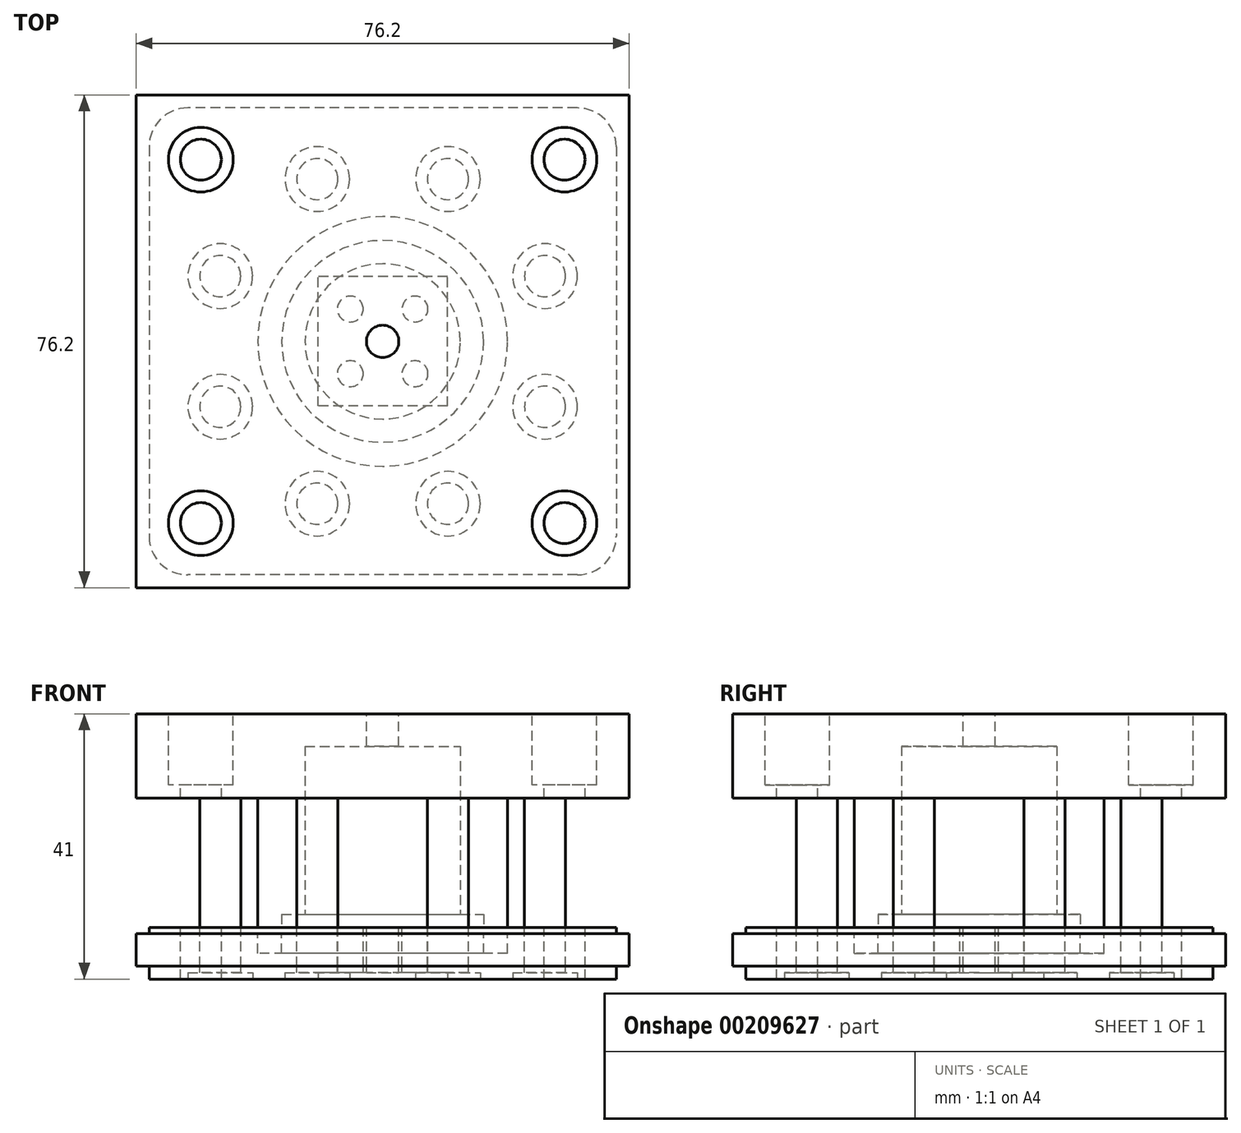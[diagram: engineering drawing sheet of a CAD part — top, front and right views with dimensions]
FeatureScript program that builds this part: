
annotation { "Feature Type Name" : "Feature", "Feature Type Description" : "" }
export const myFeature = defineFeature(function(context is Context, id is Id, definition is map)
    precondition{}
    {
        {
            var Q0;
            Q0=qCreatedBy(makeId("Top.planeOp"),FACE);
            var sketch = newSketch(context, id + "F0", { "sketchPlane" : qUnion([Q0])});
            skLineSegment(sketch, "E0.bottom", {"start": v(36.1, 36.1) * mm, "end": v(-36.1, 36.1) * mm});
            skLineSegment(sketch, "E0.top", {"start": v(36.1, -36.1) * mm, "end": v(-36.1, -36.1) * mm});
            skLineSegment(sketch, "E0.left", {"start": v(36.1, 36.1) * mm, "end": v(36.1, -36.1) * mm});
            skLineSegment(sketch, "E0.right", {"start": v(-36.1, 36.1) * mm, "end": v(-36.1, -36.1) * mm});
            skPoint(sketch, "E0.middle", {"position": v(0, 0) * mm});
            skSolve(sketch);
        }
        {
            var Q0;
            Q0=makeQuery(id+"F0.imprint","IMPRINT",FACE,{"disambiguationData":[TD([[makeQuery(id+"F0.imprint","IMPRINT",EDGE,{"derivedFrom":sQuery(id+"F0.wireOp",EDGE,"E0.bottom")}),1.0]])]});
            extrude(context, id + "F1", {"entities" : qUnion([Q0]), "depth" : 2 * mm});
        }
        {
            var Q0;
            Q0=makeQuery(id+"F1.opExtrude","SWEPT_EDGE",EDGE,{"disambiguationData":[OSD([sQuery(id+"F0.wireOp",EDGE,"E0.top"),sQuery(id+"F0.wireOp",EDGE,"E0.right")])]});
            var Q1;
            Q1=makeQuery(id+"F1.opExtrude","SWEPT_EDGE",EDGE,{"disambiguationData":[OSD([sQuery(id+"F0.wireOp",EDGE,"E0.top"),sQuery(id+"F0.wireOp",EDGE,"E0.left")])]});
            var Q2;
            Q2=makeQuery(id+"F1.opExtrude","SWEPT_EDGE",EDGE,{"disambiguationData":[OSD([sQuery(id+"F0.wireOp",EDGE,"E0.bottom"),sQuery(id+"F0.wireOp",EDGE,"E0.right")])]});
            var Q3;
            Q3=makeQuery(id+"F1.opExtrude","SWEPT_EDGE",EDGE,{"disambiguationData":[OSD([sQuery(id+"F0.wireOp",EDGE,"E0.bottom"),sQuery(id+"F0.wireOp",EDGE,"E0.left")])]});
            fillet(context, id + "F2", {"entities" : qUnion([Q0, Q1, Q2, Q3]), "radius" : 6 * mm, "tangentPropagation" : true, "allowEdgeOverflow" : false});
        }
        {
            var Q0;
            Q0=makeQuery(id+"F1.opExtrude","CAP_FACE",FACE,{"disambiguationData":[OSD([sQuery(id+"F0.wireOp",EDGE,"E0.bottom"),sQuery(id+"F0.wireOp",EDGE,"E0.top"),sQuery(id+"F0.wireOp",EDGE,"E0.left"),sQuery(id+"F0.wireOp",EDGE,"E0.right")])],"isStart":false});
            var sketch = newSketch(context, id + "F3", { "sketchPlane" : qUnion([Q0])});
            skLineSegment(sketch, "E1.bottom", {"start": v(10.1, 25.1) * mm, "end": v(-10.1, 25.1) * mm, "construction": true});
            skLineSegment(sketch, "E1.top", {"start": v(10.1, -25.1) * mm, "end": v(-10.1, -25.1) * mm});
            skLineSegment(sketch, "E1.left", {"start": v(10.1, 25.1) * mm, "end": v(10.1, -25.1) * mm, "construction": true});
            skLineSegment(sketch, "E1.right", {"start": v(-10.1, 25.1) * mm, "end": v(-10.1, -25.1) * mm, "construction": true});
            skPoint(sketch, "E1.middle", {"position": v(0, 0) * mm});
            skLineSegment(sketch, "E2.bottom", {"start": v(25.1, 10.1) * mm, "end": v(-25.1, 10.1) * mm, "construction": true});
            skLineSegment(sketch, "E2.top", {"start": v(25.1, -10.1) * mm, "end": v(-25.1, -10.1) * mm, "construction": true});
            skLineSegment(sketch, "E2.left", {"start": v(25.1, 10.1) * mm, "end": v(25.1, -10.1) * mm, "construction": true});
            skLineSegment(sketch, "E2.right", {"start": v(-25.1, 10.1) * mm, "end": v(-25.1, -10.1) * mm, "construction": true});
            skLineSegment(sketch, "E3.bottom", {"start": v(28.1, 28.1) * mm, "end": v(-28.1, 28.1) * mm, "construction": true});
            skLineSegment(sketch, "E3.top", {"start": v(28.1, -28.1) * mm, "end": v(-28.1, -28.1) * mm, "construction": true});
            skLineSegment(sketch, "E3.left", {"start": v(28.1, 28.1) * mm, "end": v(28.1, -28.1) * mm, "construction": true});
            skLineSegment(sketch, "E3.right", {"start": v(-28.1, 28.1) * mm, "end": v(-28.1, -28.1) * mm, "construction": true});
            skLineSegment(sketch, "E4.bottom", {"start": v(5, 5) * mm, "end": v(-5, 5) * mm, "construction": true});
            skLineSegment(sketch, "E4.top", {"start": v(5, -5) * mm, "end": v(-5, -5) * mm, "construction": true});
            skLineSegment(sketch, "E4.left", {"start": v(5, 5) * mm, "end": v(5, -5) * mm, "construction": true});
            skLineSegment(sketch, "E4.right", {"start": v(-5, 5) * mm, "end": v(-5, -5) * mm, "construction": true});
            skCircle(sketch, "E5", {"center": v(-28.1, 28.1) * mm, "radius": 3.18 * mm});
            skCircle(sketch, "E6", {"center": v(28.1, 28.1) * mm, "radius": 3.18 * mm});
            skCircle(sketch, "E7", {"center": v(28.1, -28.1) * mm, "radius": 3.18 * mm});
            skCircle(sketch, "E8", {"center": v(25.1, 10.1) * mm, "radius": 3.18 * mm});
            skCircle(sketch, "E9", {"center": v(25.1, -10.1) * mm, "radius": 3.18 * mm});
            skCircle(sketch, "E10", {"center": v(-25.1, -10.1) * mm, "radius": 3.18 * mm});
            skCircle(sketch, "E11", {"center": v(-25.1, 10.1) * mm, "radius": 3.18 * mm});
            skCircle(sketch, "E12", {"center": v(-28.1, -28.1) * mm, "radius": 3.18 * mm});
            skCircle(sketch, "E13", {"center": v(-10.1, 25.1) * mm, "radius": 3.18 * mm});
            skCircle(sketch, "E14", {"center": v(10.1, 25.1) * mm, "radius": 3.18 * mm});
            skCircle(sketch, "E15", {"center": v(10.1, -25.1) * mm, "radius": 3.18 * mm});
            skCircle(sketch, "E16", {"center": v(-10.1, -25.1) * mm, "radius": 3.18 * mm});
            skCircle(sketch, "E17", {"center": v(5, 5) * mm, "radius": 2 * mm});
            skCircle(sketch, "E18", {"center": v(-5, 5) * mm, "radius": 2 * mm});
            skCircle(sketch, "E19", {"center": v(-5, -5) * mm, "radius": 2 * mm});
            skCircle(sketch, "E20", {"center": v(5, -5) * mm, "radius": 2 * mm});
            skSolve(sketch);
        }
        {
            var Q0;
            Q0=makeQuery(id+"F3.imprint","IMPRINT",FACE,{"disambiguationData":[TD([[makeQuery(id+"F3.imprint","IMPRINT",EDGE,{"derivedFrom":sQuery(id+"F3.wireOp",EDGE,"E5")}),1.0]])]});
            var Q1;
            Q1=makeQuery(id+"F3.imprint","IMPRINT",FACE,{"disambiguationData":[TD([[makeQuery(id+"F3.imprint","IMPRINT",EDGE,{"derivedFrom":sQuery(id+"F3.wireOp",EDGE,"E13")}),1.0]])]});
            var Q2;
            Q2=makeQuery(id+"F3.imprint","IMPRINT",FACE,{"disambiguationData":[TD([[makeQuery(id+"F3.imprint","IMPRINT",EDGE,{"derivedFrom":sQuery(id+"F3.wireOp",EDGE,"E14")}),1.0]])]});
            var Q3;
            Q3=makeQuery(id+"F3.imprint","IMPRINT",FACE,{"disambiguationData":[TD([[makeQuery(id+"F3.imprint","IMPRINT",EDGE,{"derivedFrom":sQuery(id+"F3.wireOp",EDGE,"E6")}),1.0]])]});
            var Q4;
            Q4=makeQuery(id+"F3.imprint","IMPRINT",FACE,{"disambiguationData":[TD([[makeQuery(id+"F3.imprint","IMPRINT",EDGE,{"derivedFrom":sQuery(id+"F3.wireOp",EDGE,"E11")}),1.0]])]});
            var Q5;
            Q5=makeQuery(id+"F3.imprint","IMPRINT",FACE,{"disambiguationData":[TD([[makeQuery(id+"F3.imprint","IMPRINT",EDGE,{"derivedFrom":sQuery(id+"F3.wireOp",EDGE,"E18")}),1.0]])]});
            var Q6;
            Q6=makeQuery(id+"F3.imprint","IMPRINT",FACE,{"disambiguationData":[TD([[makeQuery(id+"F3.imprint","IMPRINT",EDGE,{"derivedFrom":sQuery(id+"F3.wireOp",EDGE,"E17")}),1.0]])]});
            var Q7;
            Q7=makeQuery(id+"F3.imprint","IMPRINT",FACE,{"disambiguationData":[TD([[makeQuery(id+"F3.imprint","IMPRINT",EDGE,{"derivedFrom":sQuery(id+"F3.wireOp",EDGE,"E8")}),1.0]])]});
            var Q8;
            Q8=makeQuery(id+"F3.imprint","IMPRINT",FACE,{"disambiguationData":[TD([[makeQuery(id+"F3.imprint","IMPRINT",EDGE,{"derivedFrom":sQuery(id+"F3.wireOp",EDGE,"E9")}),1.0]])]});
            var Q9;
            Q9=makeQuery(id+"F3.imprint","IMPRINT",FACE,{"disambiguationData":[TD([[makeQuery(id+"F3.imprint","IMPRINT",EDGE,{"derivedFrom":sQuery(id+"F3.wireOp",EDGE,"E20")}),1.0]])]});
            var Q10;
            Q10=makeQuery(id+"F3.imprint","IMPRINT",FACE,{"disambiguationData":[TD([[makeQuery(id+"F3.imprint","IMPRINT",EDGE,{"derivedFrom":sQuery(id+"F3.wireOp",EDGE,"E19")}),1.0]])]});
            var Q11;
            Q11=makeQuery(id+"F3.imprint","IMPRINT",FACE,{"disambiguationData":[TD([[makeQuery(id+"F3.imprint","IMPRINT",EDGE,{"derivedFrom":sQuery(id+"F3.wireOp",EDGE,"E10")}),1.0]])]});
            var Q12;
            Q12=makeQuery(id+"F3.imprint","IMPRINT",FACE,{"disambiguationData":[TD([[makeQuery(id+"F3.imprint","IMPRINT",EDGE,{"derivedFrom":sQuery(id+"F3.wireOp",EDGE,"E12")}),1.0]])]});
            var Q13;
            Q13=makeQuery(id+"F3.imprint","IMPRINT",FACE,{"disambiguationData":[TD([[makeQuery(id+"F3.imprint","IMPRINT",EDGE,{"derivedFrom":sQuery(id+"F3.wireOp",EDGE,"E16")}),1.0]])]});
            var Q14;
            Q14=makeQuery(id+"F3.imprint","IMPRINT",FACE,{"disambiguationData":[TD([[makeQuery(id+"F3.imprint","IMPRINT",EDGE,{"derivedFrom":sQuery(id+"F3.wireOp",EDGE,"E15")}),1.0]])]});
            var Q15;
            Q15=makeQuery(id+"F3.imprint","IMPRINT",FACE,{"disambiguationData":[TD([[makeQuery(id+"F3.imprint","IMPRINT",EDGE,{"derivedFrom":sQuery(id+"F3.wireOp",EDGE,"E7")}),1.0]])]});
            extrude(context, id + "F4", {"entities" : qUnion([Q0, Q1, Q2, Q3, Q4, Q5, Q6, Q7, Q8, Q9, Q10, Q11, Q12, Q13, Q14, Q15]), "operationType" : NewBodyOperationType.REMOVE, "endBound" : BoundingType.THROUGH_ALL, "oppositeDirection" : true, "depth" : 25 * mm});
        }
        {
            var Q0;
            Q0=makeQuery(id+"F1.opExtrude","CAP_FACE",FACE,{"disambiguationData":[OSD([sQuery(id+"F0.wireOp",EDGE,"E0.bottom"),sQuery(id+"F0.wireOp",EDGE,"E0.top"),sQuery(id+"F0.wireOp",EDGE,"E0.left"),sQuery(id+"F0.wireOp",EDGE,"E0.right")])],"isStart":true});
            var sketch = newSketch(context, id + "F5", { "sketchPlane" : qUnion([Q0])});
            skPoint(sketch, "E21.0", {"position": v(-10.1, 25.1) * mm});
            skPoint(sketch, "E21.1", {"position": v(10.1, 25.1) * mm});
            skPoint(sketch, "E21.2", {"position": v(25.1, 10.1) * mm});
            skPoint(sketch, "E21.3", {"position": v(25.1, -10.1) * mm});
            skPoint(sketch, "E21.5", {"position": v(10.1, -25.1) * mm});
            skPoint(sketch, "E21.6", {"position": v(-10.1, -25.1) * mm});
            skPoint(sketch, "E21.8", {"position": v(-25.1, -10.1) * mm});
            skPoint(sketch, "E21.9", {"position": v(-25.1, 10.1) * mm});
            skCircle(sketch, "E22", {"center": v(-10.1, 25.1) * mm, "radius": 5 * mm});
            skCircle(sketch, "E23", {"center": v(10.1, 25.1) * mm, "radius": 5 * mm});
            skCircle(sketch, "E24", {"center": v(25.1, 10.1) * mm, "radius": 5 * mm});
            skCircle(sketch, "E25", {"center": v(25.1, -10.1) * mm, "radius": 5 * mm});
            skCircle(sketch, "E26", {"center": v(10.1, -25.1) * mm, "radius": 5 * mm});
            skCircle(sketch, "E27", {"center": v(-10.1, -25.1) * mm, "radius": 5 * mm});
            skCircle(sketch, "E28", {"center": v(-25.1, -10.1) * mm, "radius": 5 * mm});
            skCircle(sketch, "E29", {"center": v(-25.1, 10.1) * mm, "radius": 5 * mm});
            skLineSegment(sketch, "E30.bottom", {"start": v(10, 10) * mm, "end": v(-10, 10) * mm});
            skLineSegment(sketch, "E30.top", {"start": v(10, -10) * mm, "end": v(-10, -10) * mm});
            skLineSegment(sketch, "E30.left", {"start": v(10, 10) * mm, "end": v(10, -10) * mm});
            skLineSegment(sketch, "E30.right", {"start": v(-10, 10) * mm, "end": v(-10, -10) * mm});
            skPoint(sketch, "E30.middle", {"position": v(0, 0) * mm});
            skSolve(sketch);
        }
        {
            var Q0;
            Q0=makeQuery(id+"F5.imprint","IMPRINT",FACE,{"disambiguationData":[TD([[makeQuery(id+"F5.imprint","IMPRINT",EDGE,{"derivedFrom":sQuery(id+"F5.wireOp",EDGE,"E22")}),1.0]])]});
            var Q1;
            Q1=makeQuery(id+"F5.imprint","IMPRINT",FACE,{"disambiguationData":[TD([[makeQuery(id+"F5.imprint","IMPRINT",EDGE,{"derivedFrom":sQuery(id+"F5.wireOp",EDGE,"E23")}),1.0]])]});
            var Q2;
            Q2=makeQuery(id+"F5.imprint","IMPRINT",FACE,{"disambiguationData":[TD([[makeQuery(id+"F5.imprint","IMPRINT",EDGE,{"derivedFrom":sQuery(id+"F5.wireOp",EDGE,"E24")}),1.0]])]});
            var Q3;
            Q3=makeQuery(id+"F5.imprint","IMPRINT",FACE,{"disambiguationData":[TD([[makeQuery(id+"F5.imprint","IMPRINT",EDGE,{"derivedFrom":sQuery(id+"F5.wireOp",EDGE,"E29")}),1.0]])]});
            var Q4;
            Q4=makeQuery(id+"F5.imprint","IMPRINT",FACE,{"disambiguationData":[TD([[makeQuery(id+"F5.imprint","IMPRINT",EDGE,{"derivedFrom":sQuery(id+"F5.wireOp",EDGE,"E30.bottom")}),1.0]])]});
            var Q5;
            Q5=makeQuery(id+"F5.imprint","IMPRINT",FACE,{"disambiguationData":[TD([[makeQuery(id+"F5.imprint","IMPRINT",EDGE,{"derivedFrom":sQuery(id+"F5.wireOp",EDGE,"E28")}),1.0]])]});
            var Q6;
            Q6=makeQuery(id+"F5.imprint","IMPRINT",FACE,{"disambiguationData":[TD([[makeQuery(id+"F5.imprint","IMPRINT",EDGE,{"derivedFrom":sQuery(id+"F5.wireOp",EDGE,"E27")}),1.0]])]});
            var Q7;
            Q7=makeQuery(id+"F5.imprint","IMPRINT",FACE,{"disambiguationData":[TD([[makeQuery(id+"F5.imprint","IMPRINT",EDGE,{"derivedFrom":sQuery(id+"F5.wireOp",EDGE,"E26")}),1.0]])]});
            var Q8;
            Q8=makeQuery(id+"F5.imprint","IMPRINT",FACE,{"disambiguationData":[TD([[makeQuery(id+"F5.imprint","IMPRINT",EDGE,{"derivedFrom":sQuery(id+"F5.wireOp",EDGE,"E25")}),1.0]])]});
            extrude(context, id + "F6", {"entities" : qUnion([Q0, Q1, Q2, Q3, Q4, Q5, Q6, Q7, Q8]), "operationType" : NewBodyOperationType.REMOVE, "oppositeDirection" : true, "depth" : 1 * mm});
        }
        {
            var Q0;
            Q0=makeQuery(id+"F1.opExtrude","CAP_FACE",FACE,{"disambiguationData":[OSD([sQuery(id+"F0.wireOp",EDGE,"E0.bottom"),sQuery(id+"F0.wireOp",EDGE,"E0.top"),sQuery(id+"F0.wireOp",EDGE,"E0.left"),sQuery(id+"F0.wireOp",EDGE,"E0.right")])],"isStart":false});
            cPlane(context, id + "F7", {"entities" : qUnion([Q0]), "cplaneType" : CPlaneType.OFFSET, "offset" : 0 * mm, "width" : 150 * mm, "height" : 150 * mm});
        }
        {
            var Q0;
            Q0=qCreatedBy(id+"F7.planeOp",FACE);
            var sketch = newSketch(context, id + "F8", { "sketchPlane" : qUnion([Q0])});
            skLineSegment(sketch, "E31.bottom", {"start": v(38.1, 38.1) * mm, "end": v(-38.1, 38.1) * mm});
            skLineSegment(sketch, "E31.top", {"start": v(38.1, -38.1) * mm, "end": v(-38.1, -38.1) * mm});
            skLineSegment(sketch, "E31.left", {"start": v(38.1, 38.1) * mm, "end": v(38.1, -38.1) * mm});
            skLineSegment(sketch, "E31.right", {"start": v(-38.1, 38.1) * mm, "end": v(-38.1, -38.1) * mm});
            skPoint(sketch, "E31.middle", {"position": v(0, 0) * mm});
            skSolve(sketch);
        }
        {
            var Q0;
            Q0=makeQuery(id+"F8.imprint","IMPRINT",FACE,{"disambiguationData":[TD([[makeQuery(id+"F8.imprint","IMPRINT",EDGE,{"derivedFrom":sQuery(id+"F8.wireOp",EDGE,"E31.bottom")}),1.0]])]});
            extrude(context, id + "F9", {"entities" : qUnion([Q0]), "depth" : 5 * mm});
        }
        {
            var Q0;
            Q0=makeQuery(id+"F9.opExtrude","CAP_FACE",FACE,{"disambiguationData":[OSD([sQuery(id+"F8.wireOp",EDGE,"E31.bottom"),sQuery(id+"F8.wireOp",EDGE,"E31.top"),sQuery(id+"F8.wireOp",EDGE,"E31.left"),sQuery(id+"F8.wireOp",EDGE,"E31.right")])],"isStart":false});
            var sketch = newSketch(context, id + "F10", { "sketchPlane" : qUnion([Q0])});
            skCircle(sketch, "E32.0", {"center": v(-28.1, 28.1) * mm, "radius": 3.18 * mm});
            skCircle(sketch, "E32.1", {"center": v(-10.1, 25.1) * mm, "radius": 3.18 * mm});
            skCircle(sketch, "E32.2", {"center": v(10.1, 25.1) * mm, "radius": 3.18 * mm});
            skCircle(sketch, "E32.3", {"center": v(28.1, 28.1) * mm, "radius": 3.18 * mm});
            skCircle(sketch, "E32.4", {"center": v(25.1, 10.1) * mm, "radius": 3.18 * mm});
            skCircle(sketch, "E32.5", {"center": v(25.1, -10.1) * mm, "radius": 3.18 * mm});
            skCircle(sketch, "E32.6", {"center": v(28.1, -28.1) * mm, "radius": 3.18 * mm});
            skCircle(sketch, "E32.7", {"center": v(10.1, -25.1) * mm, "radius": 3.18 * mm});
            skCircle(sketch, "E32.8", {"center": v(-10.1, -25.1) * mm, "radius": 3.18 * mm});
            skCircle(sketch, "E32.9", {"center": v(-28.1, -28.1) * mm, "radius": 3.18 * mm});
            skCircle(sketch, "E32.10", {"center": v(-25.1, -10.1) * mm, "radius": 3.18 * mm});
            skCircle(sketch, "E32.11", {"center": v(-25.1, 10.1) * mm, "radius": 3.18 * mm});
            skPoint(sketch, "E32.12", {"position": v(-5, 5) * mm});
            skPoint(sketch, "E32.13", {"position": v(-5, -5) * mm});
            skPoint(sketch, "E32.14", {"position": v(5, -5) * mm});
            skPoint(sketch, "E32.15", {"position": v(5, 5) * mm});
            skCircle(sketch, "E33", {"center": v(-5, 5) * mm, "radius": 0.1 * mm});
            skCircle(sketch, "E34", {"center": v(-5, -5) * mm, "radius": 0.1 * mm});
            skCircle(sketch, "E35", {"center": v(5, 5) * mm, "radius": 0.1 * mm});
            skCircle(sketch, "E36", {"center": v(5, -5) * mm, "radius": 0.1 * mm});
            skCircle(sketch, "E37", {"center": v(-5, 5) * mm, "radius": 1 * mm});
            skCircle(sketch, "E38", {"center": v(-5, -5) * mm, "radius": 1 * mm});
            skCircle(sketch, "E39", {"center": v(5, 5) * mm, "radius": 1 * mm});
            skCircle(sketch, "E40", {"center": v(5, -5) * mm, "radius": 1 * mm});
            skCircle(sketch, "E41", {"center": v(0, 0) * mm, "radius": 15.6 * mm});
            skCircle(sketch, "E42", {"center": v(0, 0) * mm, "radius": 19.3 * mm});
            skSolve(sketch);
        }
        {
            var Q0;
            Q0=makeQuery(id+"F10.imprint","IMPRINT",FACE,{"disambiguationData":[TD([[makeQuery(id+"F10.imprint","IMPRINT",EDGE,{"derivedFrom":sQuery(id+"F10.wireOp",EDGE,"E33")}),1.0]])]});
            var Q1;
            Q1=makeQuery(id+"F10.imprint","IMPRINT",FACE,{"disambiguationData":[TD([[makeQuery(id+"F10.imprint","IMPRINT",EDGE,{"derivedFrom":sQuery(id+"F10.wireOp",EDGE,"E34")}),1.0]])]});
            var Q2;
            Q2=makeQuery(id+"F10.imprint","IMPRINT",FACE,{"disambiguationData":[TD([[makeQuery(id+"F10.imprint","IMPRINT",EDGE,{"derivedFrom":sQuery(id+"F10.wireOp",EDGE,"E36")}),1.0]])]});
            var Q3;
            Q3=makeQuery(id+"F10.imprint","IMPRINT",FACE,{"disambiguationData":[TD([[makeQuery(id+"F10.imprint","IMPRINT",EDGE,{"derivedFrom":sQuery(id+"F10.wireOp",EDGE,"E35")}),1.0]])]});
            var Q4;
            Q4=makeQuery(id+"F10.imprint","IMPRINT",FACE,{"disambiguationData":[TD([[makeQuery(id+"F10.imprint","IMPRINT",EDGE,{"derivedFrom":sQuery(id+"F10.wireOp",EDGE,"E32.0")}),1.0]])]});
            var Q5;
            Q5=makeQuery(id+"F10.imprint","IMPRINT",FACE,{"disambiguationData":[TD([[makeQuery(id+"F10.imprint","IMPRINT",EDGE,{"derivedFrom":sQuery(id+"F10.wireOp",EDGE,"E32.1")}),1.0]])]});
            var Q6;
            Q6=makeQuery(id+"F10.imprint","IMPRINT",FACE,{"disambiguationData":[TD([[makeQuery(id+"F10.imprint","IMPRINT",EDGE,{"derivedFrom":sQuery(id+"F10.wireOp",EDGE,"E32.2")}),1.0]])]});
            var Q7;
            Q7=makeQuery(id+"F10.imprint","IMPRINT",FACE,{"disambiguationData":[TD([[makeQuery(id+"F10.imprint","IMPRINT",EDGE,{"derivedFrom":sQuery(id+"F10.wireOp",EDGE,"E32.3")}),1.0]])]});
            var Q8;
            Q8=makeQuery(id+"F10.imprint","IMPRINT",FACE,{"disambiguationData":[TD([[makeQuery(id+"F10.imprint","IMPRINT",EDGE,{"derivedFrom":sQuery(id+"F10.wireOp",EDGE,"E32.4")}),1.0]])]});
            var Q9;
            Q9=makeQuery(id+"F10.imprint","IMPRINT",FACE,{"disambiguationData":[TD([[makeQuery(id+"F10.imprint","IMPRINT",EDGE,{"derivedFrom":sQuery(id+"F10.wireOp",EDGE,"E32.5")}),1.0]])]});
            var Q10;
            Q10=makeQuery(id+"F10.imprint","IMPRINT",FACE,{"disambiguationData":[TD([[makeQuery(id+"F10.imprint","IMPRINT",EDGE,{"derivedFrom":sQuery(id+"F10.wireOp",EDGE,"E32.6")}),1.0]])]});
            var Q11;
            Q11=makeQuery(id+"F10.imprint","IMPRINT",FACE,{"disambiguationData":[TD([[makeQuery(id+"F10.imprint","IMPRINT",EDGE,{"derivedFrom":sQuery(id+"F10.wireOp",EDGE,"E32.7")}),1.0]])]});
            var Q12;
            Q12=makeQuery(id+"F10.imprint","IMPRINT",FACE,{"disambiguationData":[TD([[makeQuery(id+"F10.imprint","IMPRINT",EDGE,{"derivedFrom":sQuery(id+"F10.wireOp",EDGE,"E32.8")}),1.0]])]});
            var Q13;
            Q13=makeQuery(id+"F10.imprint","IMPRINT",FACE,{"disambiguationData":[TD([[makeQuery(id+"F10.imprint","IMPRINT",EDGE,{"derivedFrom":sQuery(id+"F10.wireOp",EDGE,"E32.9")}),1.0]])]});
            var Q14;
            Q14=makeQuery(id+"F10.imprint","IMPRINT",FACE,{"disambiguationData":[TD([[makeQuery(id+"F10.imprint","IMPRINT",EDGE,{"derivedFrom":sQuery(id+"F10.wireOp",EDGE,"E32.10")}),1.0]])]});
            var Q15;
            Q15=makeQuery(id+"F10.imprint","IMPRINT",FACE,{"disambiguationData":[TD([[makeQuery(id+"F10.imprint","IMPRINT",EDGE,{"derivedFrom":sQuery(id+"F10.wireOp",EDGE,"E32.11")}),1.0]])]});
            extrude(context, id + "F11", {"entities" : qUnion([Q0, Q1, Q2, Q3, Q4, Q5, Q6, Q7, Q8, Q9, Q10, Q11, Q12, Q13, Q14, Q15]), "operationType" : NewBodyOperationType.REMOVE, "endBound" : BoundingType.THROUGH_ALL, "oppositeDirection" : true, "depth" : 25 * mm});
        }
        {
            var Q0;
            Q0=makeQuery(id+"F10.imprint","IMPRINT",FACE,{"disambiguationData":[TD([[makeQuery(id+"F10.imprint","IMPRINT",EDGE,{"derivedFrom":sQuery(id+"F10.wireOp",EDGE,"E33")}),-1.0]])]});
            var Q1;
            Q1=makeQuery(id+"F10.imprint","IMPRINT",FACE,{"disambiguationData":[TD([[makeQuery(id+"F10.imprint","IMPRINT",EDGE,{"derivedFrom":sQuery(id+"F10.wireOp",EDGE,"E35")}),-1.0]])]});
            var Q2;
            Q2=makeQuery(id+"F10.imprint","IMPRINT",FACE,{"disambiguationData":[TD([[makeQuery(id+"F10.imprint","IMPRINT",EDGE,{"derivedFrom":sQuery(id+"F10.wireOp",EDGE,"E36")}),-1.0]])]});
            var Q3;
            Q3=makeQuery(id+"F10.imprint","IMPRINT",FACE,{"disambiguationData":[TD([[makeQuery(id+"F10.imprint","IMPRINT",EDGE,{"derivedFrom":sQuery(id+"F10.wireOp",EDGE,"E34")}),-1.0]])]});
            extrude(context, id + "F12", {"entities" : qUnion([Q0, Q1, Q2, Q3]), "operationType" : NewBodyOperationType.REMOVE, "oppositeDirection" : true, "depth" : 4 * mm});
        }
        {
            var Q0;
            Q0=makeQuery(id+"F10.imprint","IMPRINT",FACE,{"disambiguationData":[TD([[makeQuery(id+"F10.imprint","IMPRINT",EDGE,{"derivedFrom":sQuery(id+"F10.wireOp",EDGE,"E41")}),-1.0]])]});
            extrude(context, id + "F13", {"entities" : qUnion([Q0]), "operationType" : NewBodyOperationType.REMOVE, "oppositeDirection" : true, "depth" : 3 * mm});
        }
        {
            var Q0;
            {var subQ0=sQuery(id+"F8.wireOp",EDGE,"E31.bottom");var subQ1=sQuery(id+"F8.wireOp",EDGE,"E31.left");var subQ2=sQuery(id+"F8.wireOp",EDGE,"E31.top");var subQ3=sQuery(id+"F8.wireOp",EDGE,"E31.right");Q0=makeQuery(id+"F13.boolean.opBoolean","SPLIT",FACE,{"disambiguationData":[TD([makeQuery(id+"F9.opExtrude","SWEPT_FACE",FACE,{"disambiguationData":[OSD([subQ0])]})])],"derivedFrom":makeQuery(id+"F9.opExtrude","CAP_FACE",FACE,{"disambiguationData":[OSD([subQ0,subQ2,subQ1,subQ3])],"isStart":false})});}
            cPlane(context, id + "F14", {"entities" : qUnion([Q0]), "cplaneType" : CPlaneType.OFFSET, "offset" : 0 * mm, "width" : 150 * mm, "height" : 150 * mm});
        }
        {
            var Q0;
            Q0=qCreatedBy(id+"F14.planeOp",FACE);
            var sketch = newSketch(context, id + "F15", { "sketchPlane" : qUnion([Q0])});
            skLineSegment(sketch, "E43.0", {"start": v(36.1, 36.1) * mm, "end": v(-36.1, 36.1) * mm});
            skLineSegment(sketch, "E43.1", {"start": v(-36.1, 36.1) * mm, "end": v(-36.1, -36.1) * mm});
            skLineSegment(sketch, "E43.2", {"start": v(36.1, -36.1) * mm, "end": v(-36.1, -36.1) * mm});
            skLineSegment(sketch, "E43.3", {"start": v(36.1, 36.1) * mm, "end": v(36.1, -36.1) * mm});
            skSolve(sketch);
        }
        {
            var Q0;
            Q0=makeQuery(id+"F15.imprint","IMPRINT",FACE,{"disambiguationData":[TD([[makeQuery(id+"F15.imprint","IMPRINT",EDGE,{"derivedFrom":sQuery(id+"F15.wireOp",EDGE,"E43.0")}),1.0]])]});
            extrude(context, id + "F16", {"entities" : qUnion([Q0]), "depth" : 1 * mm});
        }
        {
            var Q0;
            Q0=makeQuery(id+"F16.opExtrude","CAP_FACE",FACE,{"disambiguationData":[OSD([sQuery(id+"F15.wireOp",EDGE,"E43.0"),sQuery(id+"F15.wireOp",EDGE,"E43.1"),sQuery(id+"F15.wireOp",EDGE,"E43.2"),sQuery(id+"F15.wireOp",EDGE,"E43.3")])],"isStart":false});
            var sketch = newSketch(context, id + "F17", { "sketchPlane" : qUnion([Q0])});
            skCircle(sketch, "E44.0", {"center": v(-28.1, 28.1) * mm, "radius": 3.18 * mm});
            skCircle(sketch, "E44.1", {"center": v(-10.1, 25.1) * mm, "radius": 3.18 * mm});
            skCircle(sketch, "E44.2", {"center": v(10.1, 25.1) * mm, "radius": 3.18 * mm});
            skCircle(sketch, "E44.3", {"center": v(28.1, 28.1) * mm, "radius": 3.18 * mm});
            skCircle(sketch, "E44.4", {"center": v(25.1, 10.1) * mm, "radius": 3.18 * mm});
            skCircle(sketch, "E44.5", {"center": v(5, 5) * mm, "radius": 2 * mm});
            skCircle(sketch, "E44.6", {"center": v(-5, 5) * mm, "radius": 2 * mm});
            skCircle(sketch, "E44.7", {"center": v(-25.1, 10.1) * mm, "radius": 3.18 * mm});
            skCircle(sketch, "E44.8", {"center": v(-25.1, -10.1) * mm, "radius": 3.18 * mm});
            skCircle(sketch, "E44.9", {"center": v(-5, -5) * mm, "radius": 2 * mm});
            skCircle(sketch, "E44.10", {"center": v(5, -5) * mm, "radius": 2 * mm});
            skCircle(sketch, "E44.11", {"center": v(25.1, -10.1) * mm, "radius": 3.18 * mm});
            skCircle(sketch, "E44.12", {"center": v(28.1, -28.1) * mm, "radius": 3.18 * mm});
            skCircle(sketch, "E44.13", {"center": v(10.1, -25.1) * mm, "radius": 3.18 * mm});
            skCircle(sketch, "E44.14", {"center": v(-10.1, -25.1) * mm, "radius": 3.18 * mm});
            skCircle(sketch, "E44.15", {"center": v(-28.1, -28.1) * mm, "radius": 3.18 * mm});
            skSolve(sketch);
        }
        {
            var Q0;
            Q0=makeQuery(id+"F17.imprint","IMPRINT",FACE,{"disambiguationData":[TD([[makeQuery(id+"F17.imprint","IMPRINT",EDGE,{"derivedFrom":sQuery(id+"F17.wireOp",EDGE,"E44.1")}),1.0]])]});
            var Q1;
            Q1=makeQuery(id+"F17.imprint","IMPRINT",FACE,{"disambiguationData":[TD([[makeQuery(id+"F17.imprint","IMPRINT",EDGE,{"derivedFrom":sQuery(id+"F17.wireOp",EDGE,"E44.7")}),1.0]])]});
            var Q2;
            Q2=makeQuery(id+"F17.imprint","IMPRINT",FACE,{"disambiguationData":[TD([[makeQuery(id+"F17.imprint","IMPRINT",EDGE,{"derivedFrom":sQuery(id+"F17.wireOp",EDGE,"E44.9")}),1.0]])]});
            var Q3;
            Q3=makeQuery(id+"F17.imprint","IMPRINT",FACE,{"disambiguationData":[TD([[makeQuery(id+"F17.imprint","IMPRINT",EDGE,{"derivedFrom":sQuery(id+"F17.wireOp",EDGE,"E44.11")}),1.0]])]});
            var Q4;
            Q4=makeQuery(id+"F17.imprint","IMPRINT",FACE,{"disambiguationData":[TD([[makeQuery(id+"F17.imprint","IMPRINT",EDGE,{"derivedFrom":sQuery(id+"F17.wireOp",EDGE,"E44.14")}),1.0]])]});
            var Q5;
            Q5=makeQuery(id+"F17.imprint","IMPRINT",FACE,{"disambiguationData":[TD([[makeQuery(id+"F17.imprint","IMPRINT",EDGE,{"derivedFrom":sQuery(id+"F17.wireOp",EDGE,"E44.0")}),1.0]])]});
            var Q6;
            Q6=makeQuery(id+"F17.imprint","IMPRINT",FACE,{"disambiguationData":[TD([[makeQuery(id+"F17.imprint","IMPRINT",EDGE,{"derivedFrom":sQuery(id+"F17.wireOp",EDGE,"E44.2")}),1.0]])]});
            var Q7;
            Q7=makeQuery(id+"F17.imprint","IMPRINT",FACE,{"disambiguationData":[TD([[makeQuery(id+"F17.imprint","IMPRINT",EDGE,{"derivedFrom":sQuery(id+"F17.wireOp",EDGE,"E44.3")}),1.0]])]});
            var Q8;
            Q8=makeQuery(id+"F17.imprint","IMPRINT",FACE,{"disambiguationData":[TD([[makeQuery(id+"F17.imprint","IMPRINT",EDGE,{"derivedFrom":sQuery(id+"F17.wireOp",EDGE,"E44.4")}),1.0]])]});
            var Q9;
            Q9=makeQuery(id+"F17.imprint","IMPRINT",FACE,{"disambiguationData":[TD([[makeQuery(id+"F17.imprint","IMPRINT",EDGE,{"derivedFrom":sQuery(id+"F17.wireOp",EDGE,"E44.5")}),1.0]])]});
            var Q10;
            Q10=makeQuery(id+"F17.imprint","IMPRINT",FACE,{"disambiguationData":[TD([[makeQuery(id+"F17.imprint","IMPRINT",EDGE,{"derivedFrom":sQuery(id+"F17.wireOp",EDGE,"E44.6")}),1.0]])]});
            var Q11;
            Q11=makeQuery(id+"F17.imprint","IMPRINT",FACE,{"disambiguationData":[TD([[makeQuery(id+"F17.imprint","IMPRINT",EDGE,{"derivedFrom":sQuery(id+"F17.wireOp",EDGE,"E44.10")}),1.0]])]});
            var Q12;
            Q12=makeQuery(id+"F17.imprint","IMPRINT",FACE,{"disambiguationData":[TD([[makeQuery(id+"F17.imprint","IMPRINT",EDGE,{"derivedFrom":sQuery(id+"F17.wireOp",EDGE,"E44.13")}),1.0]])]});
            var Q13;
            Q13=makeQuery(id+"F17.imprint","IMPRINT",FACE,{"disambiguationData":[TD([[makeQuery(id+"F17.imprint","IMPRINT",EDGE,{"derivedFrom":sQuery(id+"F17.wireOp",EDGE,"E44.12")}),1.0]])]});
            var Q14;
            Q14=makeQuery(id+"F17.imprint","IMPRINT",FACE,{"disambiguationData":[TD([[makeQuery(id+"F17.imprint","IMPRINT",EDGE,{"derivedFrom":sQuery(id+"F17.wireOp",EDGE,"E44.15")}),1.0]])]});
            var Q15;
            Q15=makeQuery(id+"F17.imprint","IMPRINT",FACE,{"disambiguationData":[TD([[makeQuery(id+"F17.imprint","IMPRINT",EDGE,{"derivedFrom":sQuery(id+"F17.wireOp",EDGE,"E44.8")}),1.0]])]});
            extrude(context, id + "F18", {"entities" : qUnion([Q0, Q1, Q2, Q3, Q4, Q5, Q6, Q7, Q8, Q9, Q10, Q11, Q12, Q13, Q14, Q15]), "operationType" : NewBodyOperationType.REMOVE, "endBound" : BoundingType.THROUGH_ALL, "oppositeDirection" : true, "depth" : 25 * mm});
        }
        {
            var Q0;
            Q0=makeQuery(id+"F16.opExtrude","SWEPT_EDGE",EDGE,{"disambiguationData":[OSD([sQuery(id+"F15.wireOp",EDGE,"E43.1"),sQuery(id+"F15.wireOp",EDGE,"E43.2")])]});
            var Q1;
            Q1=makeQuery(id+"F16.opExtrude","SWEPT_EDGE",EDGE,{"disambiguationData":[OSD([sQuery(id+"F15.wireOp",EDGE,"E43.2"),sQuery(id+"F15.wireOp",EDGE,"E43.3")])]});
            var Q2;
            Q2=makeQuery(id+"F16.opExtrude","SWEPT_EDGE",EDGE,{"disambiguationData":[OSD([sQuery(id+"F15.wireOp",EDGE,"E43.0"),sQuery(id+"F15.wireOp",EDGE,"E43.3")])]});
            var Q3;
            Q3=makeQuery(id+"F16.opExtrude","SWEPT_EDGE",EDGE,{"disambiguationData":[OSD([sQuery(id+"F15.wireOp",EDGE,"E43.0"),sQuery(id+"F15.wireOp",EDGE,"E43.1")])]});
            fillet(context, id + "F19", {"entities" : qUnion([Q0, Q1, Q2, Q3]), "radius" : 6 * mm, "tangentPropagation" : true, "allowEdgeOverflow" : false});
        }
        {
            var Q0;
            Q0=makeQuery(id+"F16.opExtrude","CAP_FACE",FACE,{"disambiguationData":[OSD([sQuery(id+"F15.wireOp",EDGE,"E43.0"),sQuery(id+"F15.wireOp",EDGE,"E43.1"),sQuery(id+"F15.wireOp",EDGE,"E43.2"),sQuery(id+"F15.wireOp",EDGE,"E43.3")])],"isStart":false});
            cPlane(context, id + "F20", {"entities" : qUnion([Q0]), "cplaneType" : CPlaneType.OFFSET, "offset" : 0 * mm, "width" : 150 * mm, "height" : 150 * mm});
        }
        {
            var Q0;
            Q0=qCreatedBy(id+"F20.planeOp",FACE);
            var sketch = newSketch(context, id + "F21", { "sketchPlane" : qUnion([Q0])});
            skLineSegment(sketch, "E45.bottom", {"start": v(38.1, 38.1) * mm, "end": v(-38.1, 38.1) * mm});
            skLineSegment(sketch, "E45.top", {"start": v(38.1, -38.1) * mm, "end": v(-38.1, -38.1) * mm});
            skLineSegment(sketch, "E45.left", {"start": v(38.1, 38.1) * mm, "end": v(38.1, -38.1) * mm});
            skLineSegment(sketch, "E45.right", {"start": v(-38.1, 38.1) * mm, "end": v(-38.1, -38.1) * mm});
            skPoint(sketch, "E45.middle", {"position": v(0, 0) * mm});
            skSolve(sketch);
        }
        {
            var Q0;
            Q0=makeQuery(id+"F21.imprint","IMPRINT",FACE,{"disambiguationData":[TD([[makeQuery(id+"F21.imprint","IMPRINT",EDGE,{"derivedFrom":sQuery(id+"F21.wireOp",EDGE,"E45.bottom")}),1.0]])]});
            extrude(context, id + "F22", {"entities" : qUnion([Q0]), "depth" : 33 * mm});
        }
        {
            var Q0;
            Q0=makeQuery(id+"F22.opExtrude","CAP_FACE",FACE,{"disambiguationData":[OSD([sQuery(id+"F21.wireOp",EDGE,"E45.bottom"),sQuery(id+"F21.wireOp",EDGE,"E45.top"),sQuery(id+"F21.wireOp",EDGE,"E45.left"),sQuery(id+"F21.wireOp",EDGE,"E45.right")])],"isStart":false});
            var sketch = newSketch(context, id + "F23", { "sketchPlane" : qUnion([Q0])});
            skCircle(sketch, "E46.0", {"center": v(-28.1, 28.1) * mm, "radius": 3.18 * mm});
            skCircle(sketch, "E46.1", {"center": v(28.1, 28.1) * mm, "radius": 3.18 * mm});
            skCircle(sketch, "E46.2", {"center": v(-28.1, -28.1) * mm, "radius": 3.18 * mm});
            skCircle(sketch, "E46.3", {"center": v(28.1, -28.1) * mm, "radius": 3.18 * mm});
            skCircle(sketch, "E47", {"center": v(0, 0) * mm, "radius": 2.5 * mm});
            skCircle(sketch, "E48", {"center": v(-28.1, 28.1) * mm, "radius": 5 * mm});
            skCircle(sketch, "E49", {"center": v(28.1, 28.1) * mm, "radius": 5 * mm});
            skCircle(sketch, "E50", {"center": v(28.1, -28.1) * mm, "radius": 5 * mm});
            skCircle(sketch, "E51", {"center": v(-28.1, -28.1) * mm, "radius": 5 * mm});
            skSolve(sketch);
        }
        {
            var Q0;
            Q0=makeQuery(id+"F23.imprint","IMPRINT",FACE,{"disambiguationData":[TD([[makeQuery(id+"F23.imprint","IMPRINT",EDGE,{"derivedFrom":sQuery(id+"F23.wireOp",EDGE,"E46.0")}),1.0]])]});
            var Q1;
            Q1=makeQuery(id+"F23.imprint","IMPRINT",FACE,{"disambiguationData":[TD([[makeQuery(id+"F23.imprint","IMPRINT",EDGE,{"derivedFrom":sQuery(id+"F23.wireOp",EDGE,"E46.1")}),1.0]])]});
            var Q2;
            Q2=makeQuery(id+"F23.imprint","IMPRINT",FACE,{"disambiguationData":[TD([[makeQuery(id+"F23.imprint","IMPRINT",EDGE,{"derivedFrom":sQuery(id+"F23.wireOp",EDGE,"E47")}),1.0]])]});
            var Q3;
            Q3=makeQuery(id+"F23.imprint","IMPRINT",FACE,{"disambiguationData":[TD([[makeQuery(id+"F23.imprint","IMPRINT",EDGE,{"derivedFrom":sQuery(id+"F23.wireOp",EDGE,"E46.2")}),1.0]])]});
            var Q4;
            Q4=makeQuery(id+"F23.imprint","IMPRINT",FACE,{"disambiguationData":[TD([[makeQuery(id+"F23.imprint","IMPRINT",EDGE,{"derivedFrom":sQuery(id+"F23.wireOp",EDGE,"E46.3")}),1.0]])]});
            extrude(context, id + "F24", {"entities" : qUnion([Q0, Q1, Q2, Q3, Q4]), "operationType" : NewBodyOperationType.REMOVE, "endBound" : BoundingType.THROUGH_ALL, "oppositeDirection" : true, "depth" : 25 * mm});
        }
        {
            var Q0;
            Q0=makeQuery(id+"F23.imprint","IMPRINT",FACE,{"disambiguationData":[TD([[makeQuery(id+"F23.imprint","IMPRINT",EDGE,{"derivedFrom":sQuery(id+"F23.wireOp",EDGE,"E46.0")}),-1.0]])]});
            var Q1;
            Q1=makeQuery(id+"F23.imprint","IMPRINT",FACE,{"disambiguationData":[TD([[makeQuery(id+"F23.imprint","IMPRINT",EDGE,{"derivedFrom":sQuery(id+"F23.wireOp",EDGE,"E46.1")}),-1.0]])]});
            var Q2;
            Q2=makeQuery(id+"F23.imprint","IMPRINT",FACE,{"disambiguationData":[TD([[makeQuery(id+"F23.imprint","IMPRINT",EDGE,{"derivedFrom":sQuery(id+"F23.wireOp",EDGE,"E46.3")}),-1.0]])]});
            var Q3;
            Q3=makeQuery(id+"F23.imprint","IMPRINT",FACE,{"disambiguationData":[TD([[makeQuery(id+"F23.imprint","IMPRINT",EDGE,{"derivedFrom":sQuery(id+"F23.wireOp",EDGE,"E46.2")}),-1.0]])]});
            extrude(context, id + "F25", {"entities" : qUnion([Q0, Q1, Q2, Q3]), "operationType" : NewBodyOperationType.REMOVE, "oppositeDirection" : true, "depth" : 11 * mm});
        }
        {
            var Q0;
            Q0=makeQuery(id+"F22.opExtrude","CAP_FACE",FACE,{"disambiguationData":[OSD([sQuery(id+"F21.wireOp",EDGE,"E45.bottom"),sQuery(id+"F21.wireOp",EDGE,"E45.top"),sQuery(id+"F21.wireOp",EDGE,"E45.left"),sQuery(id+"F21.wireOp",EDGE,"E45.right")])],"isStart":true});
            var sketch = newSketch(context, id + "F26", { "sketchPlane" : qUnion([Q0])});
            skCircle(sketch, "E52.0", {"center": v(-10.1, 25.1) * mm, "radius": 3.18 * mm});
            skCircle(sketch, "E52.1", {"center": v(10.1, 25.1) * mm, "radius": 3.18 * mm});
            skCircle(sketch, "E52.2", {"center": v(25.1, 10.1) * mm, "radius": 3.18 * mm});
            skCircle(sketch, "E52.3", {"center": v(25.1, -10.1) * mm, "radius": 3.18 * mm});
            skCircle(sketch, "E52.4", {"center": v(10.1, -25.1) * mm, "radius": 3.18 * mm});
            skCircle(sketch, "E52.5", {"center": v(-10.1, -25.1) * mm, "radius": 3.18 * mm});
            skCircle(sketch, "E52.6", {"center": v(-25.1, -10.1) * mm, "radius": 3.18 * mm});
            skCircle(sketch, "E52.7", {"center": v(-25.1, 10.1) * mm, "radius": 3.18 * mm});
            skCircle(sketch, "E53.0", {"center": v(0, 0) * mm, "radius": 15.6 * mm});
            skCircle(sketch, "E53.1", {"center": v(0, 0) * mm, "radius": 19.3 * mm});
            skCircle(sketch, "E54", {"center": v(0, 0) * mm, "radius": 12 * mm});
            skSolve(sketch);
        }
        {
            var Q0;
            Q0=makeQuery(id+"F26.imprint","IMPRINT",FACE,{"disambiguationData":[TD([[makeQuery(id+"F26.imprint","IMPRINT",EDGE,{"derivedFrom":sQuery(id+"F26.wireOp",EDGE,"E52.0")}),-1.0]])]});
            var Q1;
            Q1=makeQuery(id+"F26.imprint","IMPRINT",FACE,{"disambiguationData":[TD([[makeQuery(id+"F26.imprint","IMPRINT",EDGE,{"derivedFrom":sQuery(id+"F26.wireOp",EDGE,"E52.1")}),-1.0]])]});
            var Q2;
            Q2=makeQuery(id+"F26.imprint","IMPRINT",FACE,{"disambiguationData":[TD([[makeQuery(id+"F26.imprint","IMPRINT",EDGE,{"derivedFrom":sQuery(id+"F26.wireOp",EDGE,"E52.2")}),-1.0]])]});
            var Q3;
            Q3=makeQuery(id+"F26.imprint","IMPRINT",FACE,{"disambiguationData":[TD([[makeQuery(id+"F26.imprint","IMPRINT",EDGE,{"derivedFrom":sQuery(id+"F26.wireOp",EDGE,"E52.3")}),-1.0]])]});
            var Q4;
            Q4=makeQuery(id+"F26.imprint","IMPRINT",FACE,{"disambiguationData":[TD([[makeQuery(id+"F26.imprint","IMPRINT",EDGE,{"derivedFrom":sQuery(id+"F26.wireOp",EDGE,"E52.4")}),-1.0]])]});
            var Q5;
            Q5=makeQuery(id+"F26.imprint","IMPRINT",FACE,{"disambiguationData":[TD([[makeQuery(id+"F26.imprint","IMPRINT",EDGE,{"derivedFrom":sQuery(id+"F26.wireOp",EDGE,"E52.5")}),-1.0]])]});
            var Q6;
            Q6=makeQuery(id+"F26.imprint","IMPRINT",FACE,{"disambiguationData":[TD([[makeQuery(id+"F26.imprint","IMPRINT",EDGE,{"derivedFrom":sQuery(id+"F26.wireOp",EDGE,"E52.6")}),-1.0]])]});
            var Q7;
            Q7=makeQuery(id+"F26.imprint","IMPRINT",FACE,{"disambiguationData":[TD([[makeQuery(id+"F26.imprint","IMPRINT",EDGE,{"derivedFrom":sQuery(id+"F26.wireOp",EDGE,"E52.7")}),-1.0]])]});
            extrude(context, id + "F27", {"entities" : qUnion([Q0, Q1, Q2, Q3, Q4, Q5, Q6, Q7]), "operationType" : NewBodyOperationType.REMOVE, "oppositeDirection" : true, "depth" : 20 * mm});
        }
        {
            var Q0;
            Q0=makeQuery(id+"F26.imprint","IMPRINT",FACE,{"disambiguationData":[TD([[makeQuery(id+"F26.imprint","IMPRINT",EDGE,{"derivedFrom":sQuery(id+"F26.wireOp",EDGE,"E53.0")}),1.0]])]});
            extrude(context, id + "F28", {"entities" : qUnion([Q0]), "operationType" : NewBodyOperationType.REMOVE, "oppositeDirection" : true, "depth" : 2 * mm});
        }
        {
            var Q0;
            Q0=makeQuery(id+"F26.imprint","IMPRINT",FACE,{"disambiguationData":[TD([[makeQuery(id+"F26.imprint","IMPRINT",EDGE,{"derivedFrom":sQuery(id+"F26.wireOp",EDGE,"E54")}),1.0]])]});
            extrude(context, id + "F29", {"entities" : qUnion([Q0]), "operationType" : NewBodyOperationType.REMOVE, "oppositeDirection" : true, "depth" : 28 * mm});
        }
    });
